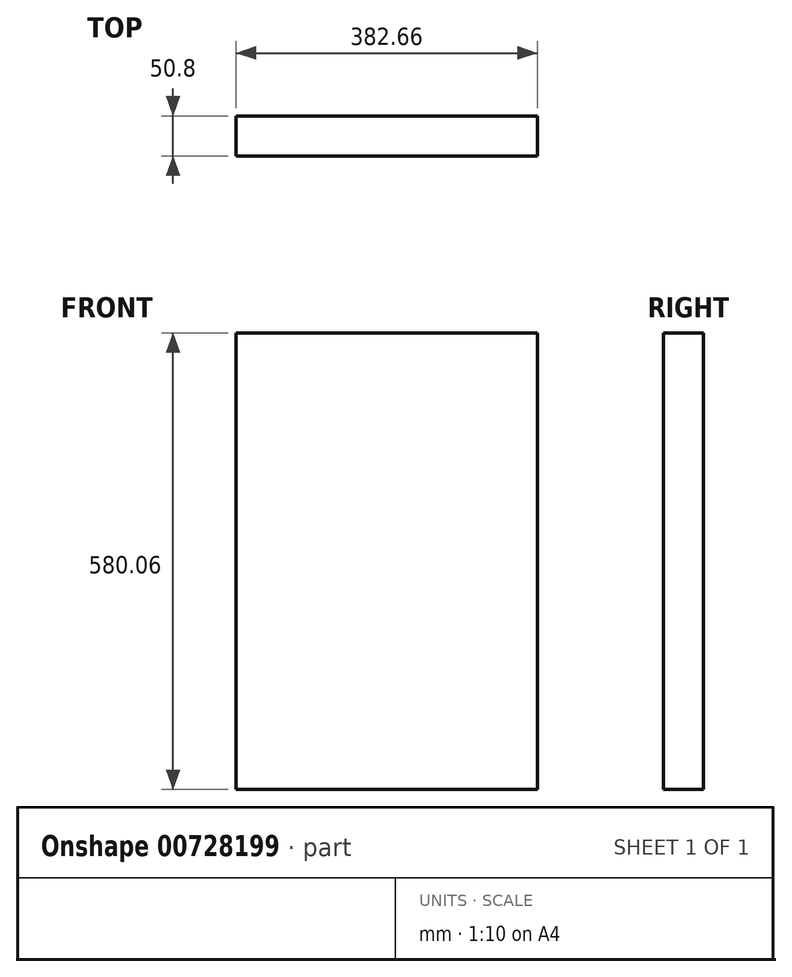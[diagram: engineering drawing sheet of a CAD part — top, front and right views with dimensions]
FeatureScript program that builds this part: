
annotation { "Feature Type Name" : "Feature", "Feature Type Description" : "" }
export const myFeature = defineFeature(function(context is Context, id is Id, definition is map)
    precondition{}
    {
        {
            var Q0;
            Q0=qCreatedBy(makeId("Front.planeOp"),FACE);
            var sketch = newSketch(context, id + "F0", { "sketchPlane" : qUnion([Q0])});
            skLineSegment(sketch, "E0.bottom", {"start": v(-51.63, 48.73) * mm, "end": v(51.63, 48.73) * mm});
            skLineSegment(sketch, "E0.top", {"start": v(-51.63, -48.73) * mm, "end": v(51.63, -48.73) * mm});
            skLineSegment(sketch, "E0.left", {"start": v(-51.63, 48.73) * mm, "end": v(-51.63, -48.73) * mm});
            skLineSegment(sketch, "E0.right", {"start": v(51.63, 48.73) * mm, "end": v(51.63, -48.73) * mm});
            skPoint(sketch, "E0.middle", {"position": v(0, 0) * mm});
            skSolve(sketch);
        }
        {
            var Q0;
            Q0=makeQuery(id+"F0.imprint","IMPRINT",FACE,{"disambiguationData":[TD([[makeQuery(id+"F0.imprint","IMPRINT",EDGE,{"derivedFrom":sQuery(id+"F0.wireOp",EDGE,"E0.bottom")}),-1.0]])]});
            extrude(context, id + "F1", {"entities" : qUnion([Q0]), "depth" : 50.8 * mm, "offsetDistance" : 25.4 * mm});
        }
        {
            var Q0;
            Q0=makeQuery(id+"F1.opExtrude","SWEPT_FACE",FACE,{"disambiguationData":[OSD([sQuery(id+"F0.wireOp",EDGE,"E0.right")])]});
            extrude(context, id + "F2", {"entities" : qUnion([Q0]), "operationType" : NewBodyOperationType.ADD, "depth" : 279.4 * mm, "offsetDistance" : 25.4 * mm});
        }
        {
            var Q0;
            {var subQ0=sQuery(id+"F0.wireOp",EDGE,"E0.bottom");Q0=makeQuery(id+"F2.boolean.opBoolean","MERGE",FACE,{"derivedFrom":[makeQuery(id+"F1.opExtrude","SWEPT_FACE",FACE,{"disambiguationData":[OSD([subQ0])]}),makeQuery(id+"F2.opExtrude","SWEPT_FACE",FACE,{"disambiguationData":[OSD([subQ0,sQuery(id+"F0.wireOp",EDGE,"E0.right")])]})]});}
            extrude(context, id + "F3", {"entities" : qUnion([Q0]), "operationType" : NewBodyOperationType.ADD, "depth" : 482.6 * mm, "offsetDistance" : 25.4 * mm});
        }
    });
